# Revit family: Electrical_Equipment-Floor_Box-Hubbell_Wiring-AFBS1R6FF
name_source: partatom
category: Electrical Fixtures
revit_build: Autodesk Revit 2015 (Build: 20140606_1530(x64)
units: mm (PartAtom-declared; Revit-internal decimal feet)

## types (1)
- AFBS1R6FF
    Assembly Code = D5020115
    Conduit Connector 1 Radius = 0.75 "
    Conduit Connector 2 Radius = 1.25 "
    Conduit Connector 3 Radius = 0.5 "
    Conduit Connector_1 Description = 0.75in. NPT Power Hub
    Conduit Connector_2 Description = 1.25in. NPT Data Hub
    Conduit Connector_3 Description = 0.75in. and 0.5in. NPT Power Hub
    Default Elevation = 48 "
    Description = Raised Access Furniture Feed Floor Box
    Manufacturer = Hubbell Wiring Device-Kellems
    Manufacturer Fax = 203-882-4852
    Model = AFBS1R6BASE
    Product Documentation Link = http://www.hubbell-wiring.com
    Product Material = Metal-Hubbell-Galzanized Steel
    Product Page URL = http://www.hubbell-wiring.com
    Product data url = https://bimobject.com
    URL = http://www.hubbell-wiring.com

## geometry (parser evidence)
native form markers: Blend x25, Sweep x5
no freeform markers — native parametric forms only
